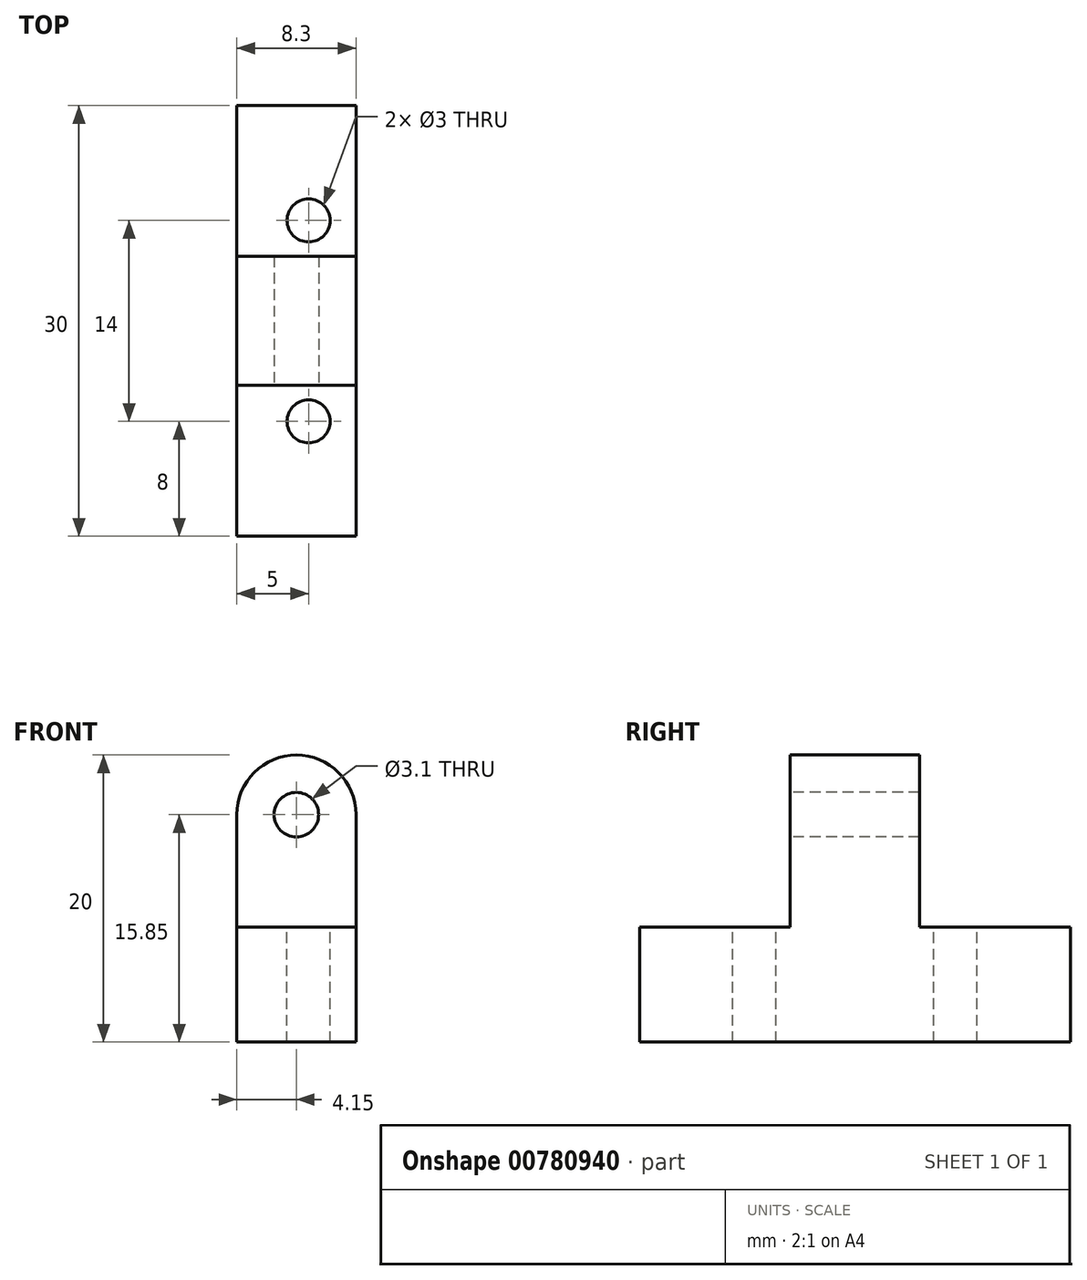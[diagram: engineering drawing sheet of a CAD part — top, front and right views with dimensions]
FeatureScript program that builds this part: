
annotation { "Feature Type Name" : "Feature", "Feature Type Description" : "" }
export const myFeature = defineFeature(function(context is Context, id is Id, definition is map)
    precondition{}
    {
        {
            var Q0;
            Q0=qCreatedBy(makeId("Top.planeOp"),FACE);
            var sketch = newSketch(context, id + "F0", { "sketchPlane" : qUnion([Q0])});
            skLineSegment(sketch, "E0.bottom", {"start": v(4.15, -15) * mm, "end": v(-4.15, -15) * mm});
            skLineSegment(sketch, "E0.top", {"start": v(4.15, 15) * mm, "end": v(-4.15, 15) * mm});
            skLineSegment(sketch, "E0.left", {"start": v(4.15, -15) * mm, "end": v(4.15, 15) * mm});
            skLineSegment(sketch, "E0.right", {"start": v(-4.15, -15) * mm, "end": v(-4.15, 15) * mm});
            skPoint(sketch, "E0.middle", {"position": v(0, 0) * mm});
            skSolve(sketch);
        }
        {
            var Q0;
            Q0 = qSketchRegion(id + "F0", true);
            extrude(context, id + "F1", {"entities" : qUnion([Q0]), "depth" : 8 * mm, "offsetDistance" : 25 * mm});
        }
        {
            var Q0;
            Q0=makeQuery(id+"F1.opExtrude","CAP_FACE",FACE,{"disambiguationData":[OSD([sQuery(id+"F0.wireOp",EDGE,"E0.bottom"),sQuery(id+"F0.wireOp",EDGE,"E0.top"),sQuery(id+"F0.wireOp",EDGE,"E0.left"),sQuery(id+"F0.wireOp",EDGE,"E0.right")])],"isStart":false});
            var sketch = newSketch(context, id + "F2", { "sketchPlane" : qUnion([Q0])});
            skCircle(sketch, "E1", {"center": v(0.85, -7) * mm, "radius": 1.5 * mm});
            skCircle(sketch, "E2", {"center": v(0.85, 7) * mm, "radius": 1.5 * mm});
            skSolve(sketch);
        }
        {
            var Q0;
            Q0 = qSketchRegion(id + "F2", true);
            extrude(context, id + "F3", {"entities" : qUnion([Q0]), "operationType" : NewBodyOperationType.REMOVE, "endBound" : BoundingType.THROUGH_ALL, "oppositeDirection" : true, "depth" : 25 * mm, "offsetDistance" : 25 * mm});
        }
        {
            var Q0;
            Q0=makeQuery(id+"F1.opExtrude","SWEPT_FACE",FACE,{"disambiguationData":[OSD([sQuery(id+"F0.wireOp",EDGE,"E0.left")])]});
            var sketch = newSketch(context, id + "F4", { "sketchPlane" : qUnion([Q0])});
            skLineSegment(sketch, "E3.bottom", {"start": v(-4.5, 8) * mm, "end": v(4.5, 8) * mm});
            skLineSegment(sketch, "E3.top", {"start": v(-4.5, 20) * mm, "end": v(4.5, 20) * mm});
            skLineSegment(sketch, "E3.left", {"start": v(-4.5, 8) * mm, "end": v(-4.5, 20) * mm});
            skLineSegment(sketch, "E3.right", {"start": v(4.5, 8) * mm, "end": v(4.5, 20) * mm});
            skLineSegment(sketch, "E4", {"start": v(0, 8) * mm, "end": v(0, 20) * mm, "construction": true});
            skSolve(sketch);
        }
        {
            var Q0;
            Q0=makeQuery(id+"F4.imprint","IMPRINT",FACE,{"disambiguationData":[TD([[makeQuery(id+"F4.imprint","IMPRINT",EDGE,{"derivedFrom":sQuery(id+"F4.wireOp",EDGE,"E3.bottom")}),1.0]])]});
            var Q1;
            Q1=makeQuery(id+"F1.opExtrude","SWEPT_FACE",FACE,{"disambiguationData":[OSD([sQuery(id+"F0.wireOp",EDGE,"E0.right")])]});
            extrude(context, id + "F5", {"entities" : qUnion([Q0]), "operationType" : NewBodyOperationType.ADD, "endBound" : BoundingType.UP_TO_SURFACE, "oppositeDirection" : true, "depth" : 25 * mm, "endBoundEntityFace" : qUnion([Q1]), "offsetDistance" : 25 * mm});
        }
        {
            var Q0;
            Q0=makeQuery(id+"F5.opExtrude","SWEPT_FACE",FACE,{"disambiguationData":[OSD([sQuery(id+"F4.wireOp",EDGE,"E3.left")])]});
            var sketch = newSketch(context, id + "F6", { "sketchPlane" : qUnion([Q0])});
            skCircle(sketch, "E5", {"center": v(0, 15.85) * mm, "radius": 1.55 * mm});
            skPoint(sketch, "E5.centerSnap0", {"position": v(0, 20) * mm});
            skSolve(sketch);
        }
        {
            var Q0;
            Q0=makeQuery(id+"F6.imprint","IMPRINT",FACE,{"disambiguationData":[TD([[makeQuery(id+"F6.imprint","IMPRINT",EDGE,{"derivedFrom":sQuery(id+"F6.wireOp",EDGE,"E5")}),1.0]])]});
            extrude(context, id + "F7", {"entities" : qUnion([Q0]), "operationType" : NewBodyOperationType.REMOVE, "endBound" : BoundingType.THROUGH_ALL, "oppositeDirection" : true, "depth" : 25 * mm, "offsetDistance" : 25 * mm});
        }
        {
            var Q0;
            Q0=makeQuery(id+"F5.opExtrude","CAP_EDGE",EDGE,{"disambiguationData":[OSD([sQuery(id+"F4.wireOp",EDGE,"E3.top")])],"isStart":true});
            var Q1;
            Q1=makeQuery(id+"F5.opExtrude","CAP_EDGE",EDGE,{"disambiguationData":[OSD([sQuery(id+"F4.wireOp",EDGE,"E3.top")])],"isStart":false});
            fillet(context, id + "F8", {"entities" : qUnion([Q0, Q1]), "radius" : 4.15 * mm, "tangentPropagation" : true, "allowEdgeOverflow" : false});
        }
    });
